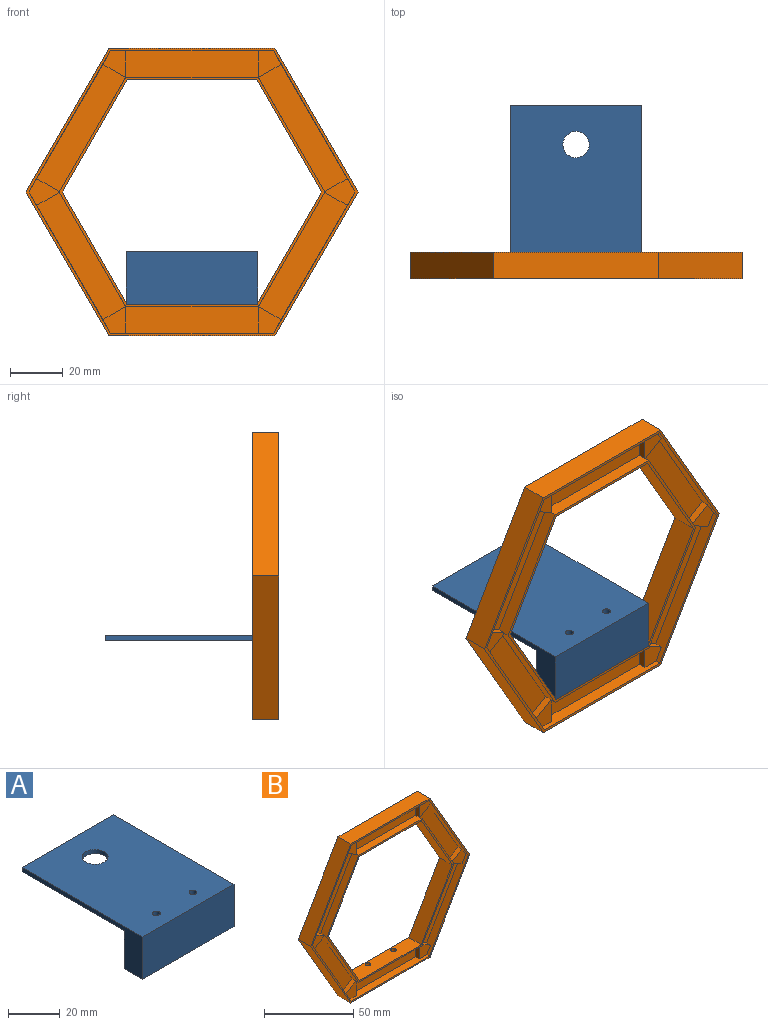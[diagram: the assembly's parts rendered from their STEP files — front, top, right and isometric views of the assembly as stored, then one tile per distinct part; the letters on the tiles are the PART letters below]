
ASSEMBLY  parts=2 mates=1
PART A: 23 faces, bbox 50x66x20 mm
  f0: plane 50x18mm, normal (0,1,0), area 864mm2, adj f1,f2,f6,f8,f9,f10,f12,f13
  f1: plane 66x20mm, normal (-1,0,0), area 312mm2, adj f0,f4,f5,f6,f7,f8
  f2: plane 66x20mm, normal (1,0,0), area 312mm2, adj f0,f4,f5,f6,f7,f8
  f3: cylinder r=5mm len=10mm, axis (0,0,-1), area 62.8mm2, adj f5,f6
  f4: plane 50x2mm, normal (0,1,0), area 100mm2, adj f1,f2,f5,f6
  f5: plane 66x50mm, normal (0,0,1), area 3207.3mm2, adj f1,f2,f3,f4,f7,f19,f21
  f6: plane 56x50mm, normal (0,0,-1), area 2721.5mm2, adj f0,f1,f2,f3,f4
  f7: plane 50x20mm, normal (0,-1,0), area 1000mm2, adj f1,f2,f5,f8
  f8: plane 50x10mm, normal (0,0,-1), area 485.9mm2, adj f0,f1,f2,f7,f20,f22
  f9: plane 5.5x3mm, normal (-1,0,0), area 16.5mm2, adj f0,f11,f12,f13
  f10: plane 5.5x3mm, normal (1,0,0), area 16.5mm2, adj f0,f11,f12,f13
  f11: plane 6x3mm, normal (0,1,0), area 18mm2, adj f9,f10,f12,f13
  f12: plane 6x5.5mm, normal (0,0,1), area 25.9mm2, adj f0,f9,f10,f11,f22
  f13: plane 6x5.5mm, normal (0,0,-1), area 25.9mm2, adj f0,f9,f10,f11,f21
  f14: plane 5.5x3mm, normal (-1,0,0), area 16.5mm2, adj f0,f16,f17,f18
  f15: plane 5.5x3mm, normal (1,0,0), area 16.5mm2, adj f0,f16,f17,f18
  f16: plane 6x3mm, normal (0,1,0), area 18mm2, adj f14,f15,f17,f18
  f17: plane 6x5.5mm, normal (0,0,1), area 25.9mm2, adj f0,f14,f15,f16,f20
  f18: plane 6x5.5mm, normal (0,0,-1), area 25.9mm2, adj f0,f14,f15,f16,f19
  f19: cylinder r=1.5mm len=6mm, axis (0,0,-1), area 56.5mm2, adj f5,f18
  f20: cylinder r=1.5mm len=11mm, axis (0,0,-1), area 103.7mm2, adj f8,f17
  f21: cylinder r=1.5mm len=6mm, axis (0,0,-1), area 56.5mm2, adj f5,f13
  f22: cylinder r=1.5mm len=11mm, axis (0,0,-1), area 103.7mm2, adj f8,f12
PART B: 53 faces, bbox 126.2x10x109.3 mm
  f0: plane 53.65x30.97mm, normal (-0.87,0,0.5), area 274.5mm2, adj f2,f8,f26,f31,f45,f46,f48,f50
  f1: plane 43.65x25.2mm, normal (0.87,0,-0.5), area 251.4mm2, adj f3,f9,f18,f31,f45,f46,f48,f50
  f2: plane 53.65x30.97mm, normal (-0.87,0,-0.5), area 274.5mm2, adj f0,f4,f26,f29,f42,f43,f45,f47
  f3: plane 43.65x25.2mm, normal (0.87,0,0.5), area 251.4mm2, adj f1,f5,f18,f29,f42,f43,f45,f47
  f4: plane 61.95x5mm, normal (0,0,-1), area 274.5mm2, adj f2,f6,f26,f28,f39,f41,f42,f44
  f5: plane 50.4x5mm, normal (0,0,1), area 251.4mm2, adj f3,f7,f18,f28,f39,f41,f42,f44
  f6: plane 53.65x30.97mm, normal (0.87,0,-0.5), area 274.5mm2, adj f4,f10,f26,f30,f33,f34,f39,f40
  f7: plane 43.65x25.2mm, normal (-0.87,0,0.5), area 251.4mm2, adj f5,f11,f18,f30,f33,f34,f39,f40
  f8: plane 61.95x5mm, normal (0,0,1), area 274.5mm2, adj f0,f10,f26,f32,f36,f37,f48,f49
  f9: plane 50.4x5mm, normal (0,0,-1), area 251.4mm2, adj f1,f11,f18,f32,f36,f37,f48,f49
  f10: plane 53.65x30.97mm, normal (0.87,0,0.5), area 274.5mm2, adj f6,f8,f26,f27,f33,f35,f36,f38
  f11: plane 43.65x25.2mm, normal (-0.87,0,-0.5), area 251.4mm2, adj f7,f9,f18,f27,f33,f35,f36,f38
  f12: plane 49.25x10mm, normal (0,0,-1), area 492.5mm2, adj f13,f17,f18,f19
  f13: plane 42.65x24.62mm, normal (-0.87,0,-0.5), area 492.5mm2, adj f12,f14,f18,f19
  f14: plane 42.65x24.62mm, normal (-0.87,0,0.5), area 492.5mm2, adj f13,f15,f18,f19
  f15: plane 49.25x10mm, normal (0,0,1), area 478.3mm2, adj f14,f16,f18,f19,f51,f52
  f16: plane 42.65x24.62mm, normal (0.87,0,0.5), area 492.5mm2, adj f15,f17,f18,f19
  f17: plane 42.65x24.62mm, normal (0.87,0,-0.5), area 492.5mm2, adj f12,f16,f18,f19
  f18: plane 100.8x87.3mm, normal (0,-1,0), area 298.9mm2, adj f1,f3,f5,f7,f9,f11,f12,f13
  f19: plane 126.2x109.3mm, normal (0,1,0), area 4044.5mm2, adj f12,f13,f14,f15,f16,f17,f20,f21
  f20: plane 54.65x31.55mm, normal (0.87,0,0.5), area 631mm2, adj f19,f21,f25,f26
  f21: plane 63.1x10mm, normal (0,0,1), area 631mm2, adj f19,f20,f22,f26
  f22: plane 54.65x31.55mm, normal (-0.87,0,0.5), area 631mm2, adj f19,f21,f23,f26
  f23: plane 54.65x31.55mm, normal (-0.87,0,-0.5), area 631mm2, adj f19,f22,f24,f26
  f24: plane 63.1x10mm, normal (0,0,-1), area 616.9mm2, adj f19,f23,f25,f26,f51,f52
  f25: plane 54.65x31.55mm, normal (0.87,0,-0.5), area 631mm2, adj f19,f20,f24,f26
  f26: plane 126.2x109.3mm, normal (0,-1,0), area 375.1mm2, adj f0,f2,f4,f6,f8,f10,f20,f21
  f27: plane 48.47x33.76mm, normal (0,-1,0), area 502mm2, adj f10,f11,f35,f38
  f28: plane 50.2x10mm, normal (0,-1,0), area 502mm2, adj f4,f5,f41,f44
  f29: plane 48.47x33.76mm, normal (0,-1,0), area 502mm2, adj f2,f3,f43,f47
  f30: plane 48.47x33.76mm, normal (0,-1,0), area 502mm2, adj f6,f7,f34,f40
  f31: plane 48.47x33.76mm, normal (0,-1,0), area 502mm2, adj f0,f1,f46,f50
  f32: plane 50.2x10mm, normal (0,-1,0), area 502mm2, adj f8,f9,f37,f49
  f33: plane 11.6x10.17mm, normal (0,-1,0), area 59.7mm2, adj f6,f7,f10,f11,f34,f35
  f34: plane 8.66x5mm, normal (0.5,0,0.87), area 30mm2, adj f6,f7,f30,f33
  f35: plane 8.66x5mm, normal (0.5,0,-0.87), area 30mm2, adj f10,f11,f27,f33
  f36: plane 10.09x8.81mm, normal (0,-1,0), area 59.7mm2, adj f8,f9,f10,f11,f37,f38
  f37: plane 10x3mm, normal (1,0,0), area 30mm2, adj f8,f9,f32,f36
  f38: plane 8.66x5mm, normal (-0.5,0,0.87), area 30mm2, adj f10,f11,f27,f36
  f39: plane 10.09x8.81mm, normal (0,-1,0), area 59.7mm2, adj f4,f5,f6,f7,f40,f41
  f40: plane 8.66x5mm, normal (-0.5,0,-0.87), area 30mm2, adj f6,f7,f30,f39
  f41: plane 10x3mm, normal (1,0,0), area 30mm2, adj f4,f5,f28,f39
  f42: plane 10.09x8.81mm, normal (0,-1,0), area 59.7mm2, adj f2,f3,f4,f5,f43,f44
  f43: plane 8.66x5mm, normal (0.5,0,-0.87), area 30mm2, adj f2,f3,f29,f42
  f44: plane 10x3mm, normal (-1,0,0), area 30mm2, adj f4,f5,f28,f42
  f45: plane 11.6x10.17mm, normal (0,-1,0), area 59.7mm2, adj f0,f1,f2,f3,f46,f47
  f46: plane 8.66x5mm, normal (-0.5,0,-0.87), area 30mm2, adj f0,f1,f31,f45
  f47: plane 8.66x5mm, normal (-0.5,0,0.87), area 30mm2, adj f2,f3,f29,f45
  f48: plane 10.09x8.81mm, normal (0,-1,0), area 59.7mm2, adj f0,f1,f8,f9,f49,f50
  f49: plane 10x3mm, normal (-1,0,0), area 30mm2, adj f8,f9,f32,f48
  f50: plane 8.66x5mm, normal (0.5,0,0.87), area 30mm2, adj f0,f1,f31,f48
  f51: cylinder r=1.5mm len=12mm, axis (0,0,1), area 113.1mm2, adj f15,f24
  f52: cylinder r=1.5mm len=12mm, axis (0,0,1), area 113.1mm2, adj f15,f24
PLACE A at identity fixed
PLACE B t=(0,-41,24.65)mm
MATE fastened B.f15 <-> A.f8  axis (0,0,1) through (0,-46.07,-18)mm
